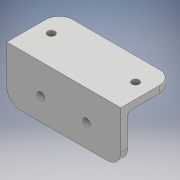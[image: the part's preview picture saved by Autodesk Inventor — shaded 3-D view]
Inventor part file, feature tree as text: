
AUTODESK INVENTOR PART (.ipt)
format: ipt  version: 2018 (Build 220112000, 112)  size: 142,336 bytes
history: native  units: mm
features: extrude x4, sketch x4, fillet x2
ambient origin geometry x8: Origin, YZ Plane, XZ Plane, XY Plane, X Axis, Y Axis, Z Axis, Center Point
bodies: Solid1 (feature_tree)
feature tree (10):
  extrude  "Extrusion1"  Depth=23.0mm
  extrude  "Extrusion2"  Depth=3.0mm
  extrude  "Extrusion3"  Depth=20.0mm
  fillet  "Fillet1"  Radius=3.2mm
  fillet  "Fillet2"  Radius=37.0mm
  extrude  "Extrusion4"  Depth=10.0mm
  sketch  "Sketch1"  dims[d0=50.0mm d1=23.0mm]
  sketch  "Sketch2"  dims[d2=3.0mm d3=0.0mm d4=3.0mm]
  sketch  "Sketch3"  dims[d5=20.0mm d6=0.0mm d7=3.2mm d8=3.2mm d9=37.0mm]
  sketch  "Sketch4"  dims[d10=6.5mm d11=10.0mm d12=10.0mm d13=20.0mm d14=0.0mm d15=6.0mm d16=2.0mm d17=3.2mm d18=3.2mm d19=10.0mm d20=20.0mm d21=15.0mm d22=20.0mm d23=0.0mm]
